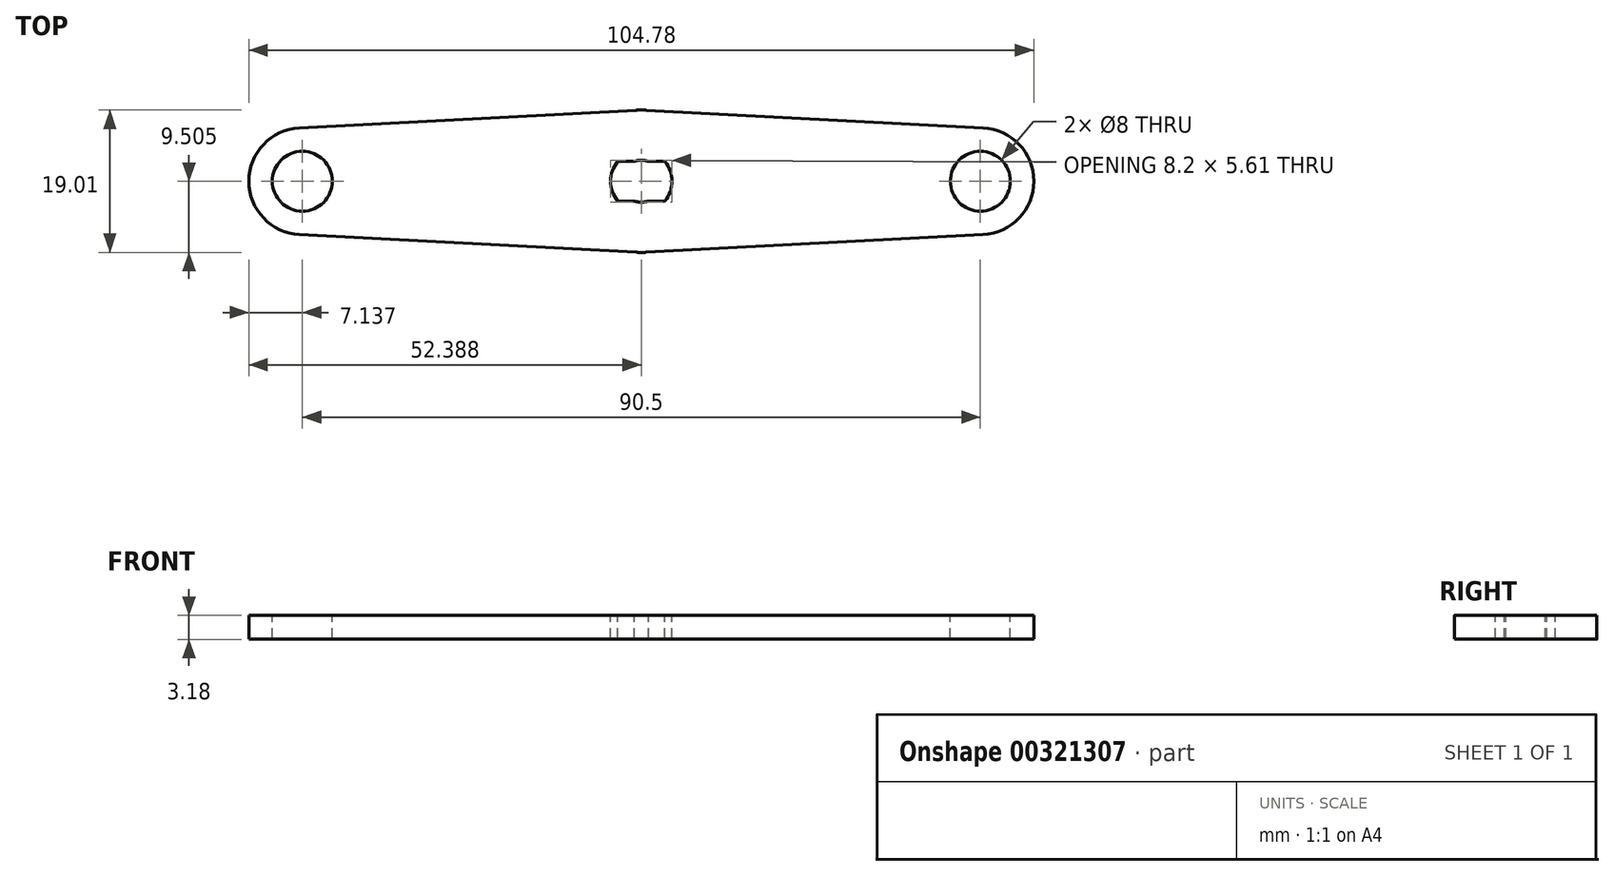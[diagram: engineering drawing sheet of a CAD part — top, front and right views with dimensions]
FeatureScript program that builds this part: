
annotation { "Feature Type Name" : "Feature", "Feature Type Description" : "" }
export const myFeature = defineFeature(function(context is Context, id is Id, definition is map)
    precondition{}
    {
        {
            var Q0;
            Q0=qCreatedBy(makeId("Top.planeOp"),FACE);
            var sketch = newSketch(context, id + "F0", { "sketchPlane" : qUnion([Q0])});
            skLineSegment(sketch, "E0.bottom", {"start": v(0, 0) * mm, "end": v(104.77, 0) * mm, "construction": true});
            skLineSegment(sketch, "E0.top", {"start": v(0, -19.05) * mm, "end": v(104.77, -19.05) * mm, "construction": true});
            skLineSegment(sketch, "E0.left", {"start": v(0, 0) * mm, "end": v(0, -19.05) * mm, "construction": true});
            skLineSegment(sketch, "E0.right", {"start": v(104.77, 0) * mm, "end": v(104.77, -19.05) * mm, "construction": true});
            skLineSegment(sketch, "E1", {"start": v(0, -9.52) * mm, "end": v(104.77, -9.52) * mm, "construction": true});
            skLineSegment(sketch, "E2", {"start": v(52.39, 0) * mm, "end": v(52.39, -19.05) * mm, "construction": true});
            skArc(sketch, "E3", {"start": v(6.76, -2.4) * mm, "mid": v(0, -9.52) * mm, "end": v(6.76, -16.65) * mm});
            skArc(sketch, "E4", {"start": v(98.01, -16.65) * mm, "mid": v(104.77, -9.52) * mm, "end": v(98.01, -2.4) * mm});
            skLineSegment(sketch, "E5", {"start": v(6.76, -2.4) * mm, "end": v(51.72, -0.04) * mm});
            skLineSegment(sketch, "E6", {"start": v(6.76, -16.65) * mm, "end": v(51.72, -19.01) * mm});
            skLineSegment(sketch, "E7", {"start": v(53.05, -19.01) * mm, "end": v(98.01, -16.65) * mm});
            skLineSegment(sketch, "E8", {"start": v(98.01, -2.4) * mm, "end": v(53.05, -0.04) * mm});
            skPoint(sketch, "E9.visualSharp", {"position": v(52.39, 0) * mm});
            skArc(sketch, "E9.filletArc", {"start": v(53.05, -0.04) * mm, "mid": v(52.39, -0.02) * mm, "end": v(51.72, -0.04) * mm});
            skPoint(sketch, "E10.visualSharp", {"position": v(52.39, -19.05) * mm});
            skArc(sketch, "E10.filletArc", {"start": v(51.72, -19.01) * mm, "mid": v(52.39, -19.03) * mm, "end": v(53.05, -19.01) * mm});
            skArc(sketch, "E11", {"start": v(49.25, -6.88) * mm, "mid": v(48.29, -9.52) * mm, "end": v(49.25, -12.17) * mm});
            skArc(sketch, "E12", {"start": v(53.34, -6.88) * mm, "mid": v(52.39, -6.72) * mm, "end": v(51.44, -6.88) * mm});
            skLineSegment(sketch, "E13.bottom", {"start": v(55.53, -6.88) * mm, "end": v(53.34, -6.88) * mm});
            skLineSegment(sketch, "E13.top", {"start": v(55.53, -12.17) * mm, "end": v(53.34, -12.17) * mm});
            skArc(sketch, "E14.trimOffspring", {"start": v(55.53, -12.17) * mm, "mid": v(56.49, -9.52) * mm, "end": v(55.53, -6.88) * mm});
            skLineSegment(sketch, "E15.trimOffspring", {"start": v(51.44, -6.88) * mm, "end": v(49.25, -6.88) * mm});
            skLineSegment(sketch, "E16.trimOffspring", {"start": v(51.44, -12.17) * mm, "end": v(49.25, -12.17) * mm});
            skArc(sketch, "E17.trimOffspring", {"start": v(51.44, -12.17) * mm, "mid": v(52.39, -12.33) * mm, "end": v(53.34, -12.17) * mm});
            skCircle(sketch, "E18", {"center": v(7.14, -9.52) * mm, "radius": 4 * mm});
            skCircle(sketch, "E19", {"center": v(97.64, -9.52) * mm, "radius": 4 * mm});
            skSolve(sketch);
        }
        {
            var Q0;
            Q0 = qSketchRegion(id + "F0", true);
            extrude(context, id + "F1", {"entities" : qUnion([Q0]), "oppositeDirection" : true, "offsetDistance" : 25.4 * mm, "depth" : 3.17 * mm});
        }
    });
